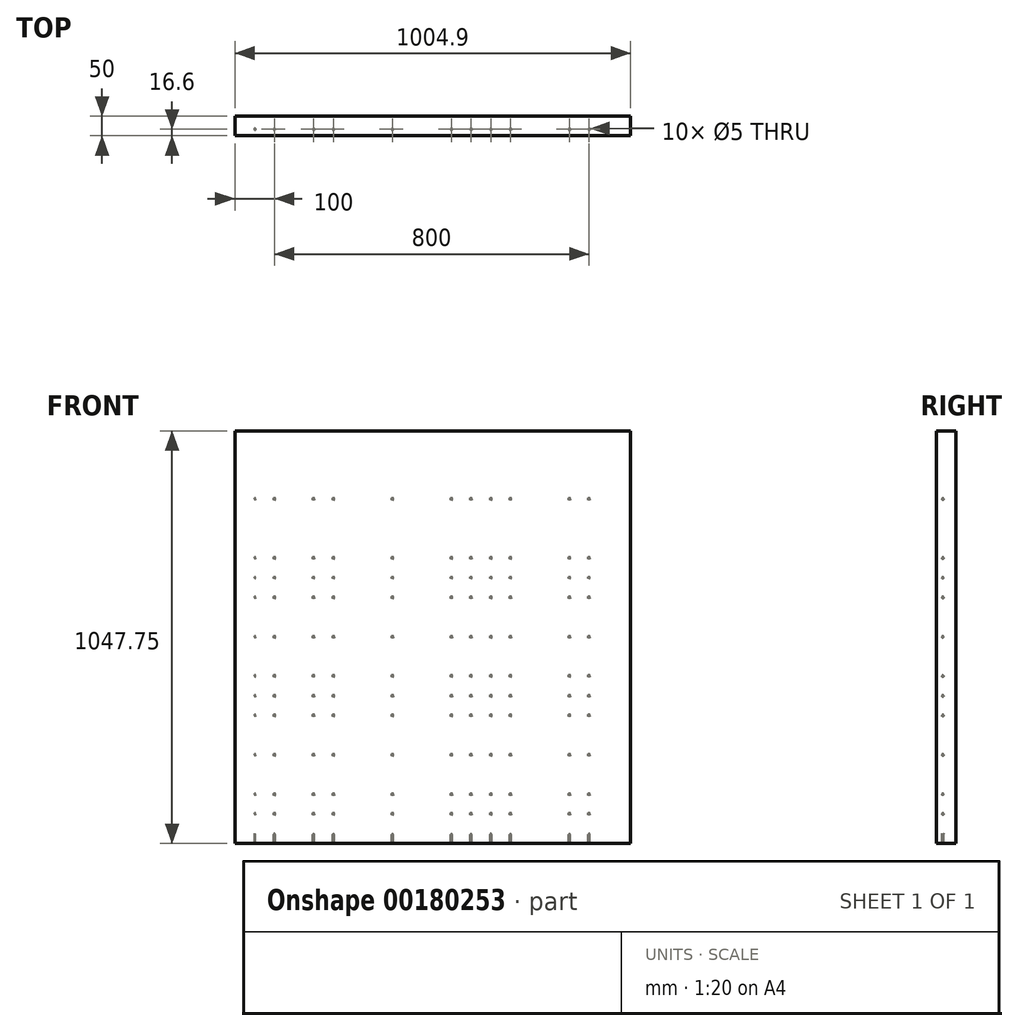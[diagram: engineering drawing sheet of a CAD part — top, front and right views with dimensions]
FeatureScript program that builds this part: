
annotation { "Feature Type Name" : "Feature", "Feature Type Description" : "" }
export const myFeature = defineFeature(function(context is Context, id is Id, definition is map)
    precondition{}
    {
        {
            var Q0;
            Q0=qCreatedBy(makeId("Right.planeOp"),FACE);
            var sketch = newSketch(context, id + "F0", { "sketchPlane" : qUnion([Q0])});
            skLineSegment(sketch, "E0.bottom", {"start": v(25, 516.75) * mm, "end": v(-25, 516.75) * mm});
            skLineSegment(sketch, "E0.top", {"start": v(25, -531) * mm, "end": v(-25, -531) * mm});
            skLineSegment(sketch, "E0.left", {"start": v(25, 516.75) * mm, "end": v(25, -531) * mm});
            skLineSegment(sketch, "E0.right", {"start": v(-25, 516.75) * mm, "end": v(-25, -531) * mm});
            skPoint(sketch, "E0.middle", {"position": v(0, -7.13) * mm});
            skLineSegment(sketch, "E1.0", {"start": v(25, -506) * mm, "end": v(-25, -506) * mm});
            skLineSegment(sketch, "E2.0", {"start": v(-8.4, 516.75) * mm, "end": v(-8.4, -531) * mm});
            skCircle(sketch, "E3", {"center": v(-8.4, -506) * mm, "radius": 2.5 * mm});
            skCircle(sketch, "E4.0.1.0", {"center": v(-8.4, -456) * mm, "radius": 2.5 * mm});
            skCircle(sketch, "E4.0.2.0", {"center": v(-8.4, -406) * mm, "radius": 2.5 * mm});
            skCircle(sketch, "E4.0.3.0", {"center": v(-8.4, -356) * mm, "radius": 2.5 * mm});
            skCircle(sketch, "E4.0.4.0", {"center": v(-8.4, -306) * mm, "radius": 2.5 * mm});
            skCircle(sketch, "E4.0.5.0", {"center": v(-8.4, -256) * mm, "radius": 2.5 * mm});
            skCircle(sketch, "E4.0.6.0", {"center": v(-8.4, -206) * mm, "radius": 2.5 * mm});
            skCircle(sketch, "E4.0.7.0", {"center": v(-8.4, -156) * mm, "radius": 2.5 * mm});
            skCircle(sketch, "E4.0.8.0", {"center": v(-8.4, -106) * mm, "radius": 2.5 * mm});
            skCircle(sketch, "E4.0.9.0", {"center": v(-8.4, -56) * mm, "radius": 2.5 * mm});
            skCircle(sketch, "E4.0.10.0", {"center": v(-8.4, -6) * mm, "radius": 2.5 * mm});
            skCircle(sketch, "E4.0.11.0", {"center": v(-8.4, 44) * mm, "radius": 2.5 * mm});
            skCircle(sketch, "E4.0.12.0", {"center": v(-8.4, 94) * mm, "radius": 2.5 * mm});
            skCircle(sketch, "E4.0.13.0", {"center": v(-8.4, 144) * mm, "radius": 2.5 * mm});
            skCircle(sketch, "E4.0.14.0", {"center": v(-8.4, 194) * mm, "radius": 2.5 * mm});
            skCircle(sketch, "E4.0.15.0", {"center": v(-8.4, 244) * mm, "radius": 2.5 * mm});
            skCircle(sketch, "E4.0.16.0", {"center": v(-8.4, 294) * mm, "radius": 2.5 * mm});
            skCircle(sketch, "E4.0.17.0", {"center": v(-8.4, 344) * mm, "radius": 2.5 * mm});
            skCircle(sketch, "E4.0.18.0", {"center": v(-8.4, 394) * mm, "radius": 2.5 * mm});
            skCircle(sketch, "E4.0.19.0", {"center": v(-8.4, 444) * mm, "radius": 2.5 * mm});
            skLineSegment(sketch, "E4.direction1", {"start": v(-8.4, -506) * mm, "end": v(16.6, -506) * mm, "construction": true});
            skLineSegment(sketch, "E4.direction2", {"start": v(-8.4, -506) * mm, "end": v(-8.4, -456) * mm, "construction": true});
            skLineSegment(sketch, "E5", {"start": v(0, 0) * mm, "end": v(63.1, 0) * mm});
            skSolve(sketch);
        }
        {
            var Q0;
            Q0=qCreatedBy(makeId("Top.planeOp"),FACE);
            cPlane(context, id + "F1", {"entities" : qUnion([Q0]), "cplaneType" : CPlaneType.OFFSET, "offset" : 466.6 * mm, "width" : 150 * mm, "height" : 150 * mm});
        }
        {
            var Q0;
            Q0=qCreatedBy(id+"F1.planeOp",FACE);
            var sketch = newSketch(context, id + "F2", { "sketchPlane" : qUnion([Q0])});
            skLineSegment(sketch, "E6.bottom", {"start": v(1004.9, -25) * mm, "end": v(0, -25) * mm});
            skLineSegment(sketch, "E6.top", {"start": v(1004.9, 25) * mm, "end": v(0, 25) * mm});
            skLineSegment(sketch, "E6.left", {"start": v(1004.9, -25) * mm, "end": v(1004.9, 25) * mm});
            skLineSegment(sketch, "E6.right", {"start": v(0, -25) * mm, "end": v(0, 25) * mm});
            skPoint(sketch, "E6.middle", {"position": v(502.45, 0) * mm});
            skLineSegment(sketch, "E7", {"start": v(0, 25) * mm, "end": v(51.84, 25) * mm});
            skLineSegment(sketch, "E8", {"start": v(0, 25) * mm, "end": v(0, 69.64) * mm});
            skLineSegment(sketch, "E9.0", {"start": v(1004.9, -8.4) * mm, "end": v(0, -8.4) * mm});
            skLineSegment(sketch, "E10.0", {"start": v(50, -25) * mm, "end": v(50, 25) * mm});
            skCircle(sketch, "E11", {"center": v(50, -8.4) * mm, "radius": 2.5 * mm});
            skCircle(sketch, "E12.1.0.0", {"center": v(100, -8.4) * mm, "radius": 2.5 * mm});
            skCircle(sketch, "E12.2.0.0", {"center": v(150, -8.4) * mm, "radius": 2.5 * mm});
            skCircle(sketch, "E12.3.0.0", {"center": v(200, -8.4) * mm, "radius": 2.5 * mm});
            skCircle(sketch, "E12.4.0.0", {"center": v(250, -8.4) * mm, "radius": 2.5 * mm});
            skCircle(sketch, "E12.5.0.0", {"center": v(300, -8.4) * mm, "radius": 2.5 * mm});
            skCircle(sketch, "E12.6.0.0", {"center": v(350, -8.4) * mm, "radius": 2.5 * mm});
            skCircle(sketch, "E12.7.0.0", {"center": v(400, -8.4) * mm, "radius": 2.5 * mm});
            skCircle(sketch, "E12.8.0.0", {"center": v(450, -8.4) * mm, "radius": 2.5 * mm});
            skCircle(sketch, "E12.9.0.0", {"center": v(500, -8.4) * mm, "radius": 2.5 * mm});
            skCircle(sketch, "E12.10.0.0", {"center": v(550, -8.4) * mm, "radius": 2.5 * mm});
            skCircle(sketch, "E12.11.0.0", {"center": v(600, -8.4) * mm, "radius": 2.5 * mm});
            skCircle(sketch, "E12.12.0.0", {"center": v(650, -8.4) * mm, "radius": 2.5 * mm});
            skCircle(sketch, "E12.13.0.0", {"center": v(700, -8.4) * mm, "radius": 2.5 * mm});
            skCircle(sketch, "E12.14.0.0", {"center": v(750, -8.4) * mm, "radius": 2.5 * mm});
            skCircle(sketch, "E12.15.0.0", {"center": v(800, -8.4) * mm, "radius": 2.5 * mm});
            skCircle(sketch, "E12.16.0.0", {"center": v(850, -8.4) * mm, "radius": 2.5 * mm});
            skCircle(sketch, "E12.17.0.0", {"center": v(900, -8.4) * mm, "radius": 2.5 * mm});
            skCircle(sketch, "E12.18.0.0", {"center": v(950, -8.4) * mm, "radius": 2.5 * mm});
            skLineSegment(sketch, "E12.direction1", {"start": v(50, -8.4) * mm, "end": v(100, -8.4) * mm, "construction": true});
            skSolve(sketch);
        }
        {
            var Q0;
            {var subQ0=sQuery(id+"F0.wireOp",EDGE,"E4.0.18.0");var subQ1=sQuery(id+"F0.wireOp",EDGE,"E2.0");var subQ2=makeQuery(id+"F0.imprint","INTERSECT",VERTEX,{"disambiguationData":[OD(0.0)],"derivedFrom":[subQ1,subQ0]});Q0=makeQuery(id+"F0.imprint","IMPRINT",FACE,{"disambiguationData":[TD([[makeQuery(id+"F0.imprint","IMPRINT",EDGE,{"disambiguationData":[TD([[subQ2,-1.0]])],"derivedFrom":subQ1}),-1.0]])]});}
            var Q1;
            {var subQ0=sQuery(id+"F0.wireOp",EDGE,"E4.0.19.0");var subQ1=sQuery(id+"F0.wireOp",EDGE,"E2.0");var subQ2=makeQuery(id+"F0.imprint","INTERSECT",VERTEX,{"disambiguationData":[OD(0.0)],"derivedFrom":[subQ1,subQ0]});Q1=makeQuery(id+"F0.imprint","IMPRINT",FACE,{"disambiguationData":[TD([[makeQuery(id+"F0.imprint","IMPRINT",EDGE,{"disambiguationData":[TD([[subQ2,-1.0]])],"derivedFrom":subQ1}),1.0]])]});}
            var Q2;
            {var subQ0=sQuery(id+"F0.wireOp",EDGE,"E4.0.19.0");var subQ1=sQuery(id+"F0.wireOp",EDGE,"E2.0");var subQ2=makeQuery(id+"F0.imprint","INTERSECT",VERTEX,{"disambiguationData":[OD(0.0)],"derivedFrom":[subQ1,subQ0]});Q2=makeQuery(id+"F0.imprint","IMPRINT",FACE,{"disambiguationData":[TD([[makeQuery(id+"F0.imprint","IMPRINT",EDGE,{"disambiguationData":[TD([[subQ2,-1.0]])],"derivedFrom":subQ1}),-1.0]])]});}
            var Q3;
            {var subQ0=sQuery(id+"F0.wireOp",EDGE,"E4.0.17.0");var subQ1=sQuery(id+"F0.wireOp",EDGE,"E2.0");var subQ2=makeQuery(id+"F0.imprint","INTERSECT",VERTEX,{"disambiguationData":[OD(0.0)],"derivedFrom":[subQ1,subQ0]});Q3=makeQuery(id+"F0.imprint","IMPRINT",FACE,{"disambiguationData":[TD([[makeQuery(id+"F0.imprint","IMPRINT",EDGE,{"disambiguationData":[TD([[subQ2,-1.0]])],"derivedFrom":subQ1}),1.0]])]});}
            var Q4;
            {var subQ0=sQuery(id+"F0.wireOp",EDGE,"E4.0.17.0");var subQ1=sQuery(id+"F0.wireOp",EDGE,"E2.0");var subQ2=makeQuery(id+"F0.imprint","INTERSECT",VERTEX,{"disambiguationData":[OD(0.0)],"derivedFrom":[subQ1,subQ0]});Q4=makeQuery(id+"F0.imprint","IMPRINT",FACE,{"disambiguationData":[TD([[makeQuery(id+"F0.imprint","IMPRINT",EDGE,{"disambiguationData":[TD([[subQ2,-1.0]])],"derivedFrom":subQ1}),-1.0]])]});}
            var Q5;
            {var subQ0=sQuery(id+"F0.wireOp",EDGE,"E4.0.18.0");var subQ1=sQuery(id+"F0.wireOp",EDGE,"E2.0");var subQ2=makeQuery(id+"F0.imprint","INTERSECT",VERTEX,{"disambiguationData":[OD(0.0)],"derivedFrom":[subQ1,subQ0]});Q5=makeQuery(id+"F0.imprint","IMPRINT",FACE,{"disambiguationData":[TD([[makeQuery(id+"F0.imprint","IMPRINT",EDGE,{"disambiguationData":[TD([[subQ2,-1.0]])],"derivedFrom":subQ1}),1.0]])]});}
            var Q6;
            {var subQ0=sQuery(id+"F0.wireOp",EDGE,"E4.0.16.0");var subQ1=sQuery(id+"F0.wireOp",EDGE,"E2.0");var subQ2=makeQuery(id+"F0.imprint","INTERSECT",VERTEX,{"disambiguationData":[OD(0.0)],"derivedFrom":[subQ1,subQ0]});Q6=makeQuery(id+"F0.imprint","IMPRINT",FACE,{"disambiguationData":[TD([[makeQuery(id+"F0.imprint","IMPRINT",EDGE,{"disambiguationData":[TD([[subQ2,-1.0]])],"derivedFrom":subQ1}),1.0]])]});}
            var Q7;
            {var subQ0=sQuery(id+"F0.wireOp",EDGE,"E4.0.16.0");var subQ1=sQuery(id+"F0.wireOp",EDGE,"E2.0");var subQ2=makeQuery(id+"F0.imprint","INTERSECT",VERTEX,{"disambiguationData":[OD(0.0)],"derivedFrom":[subQ1,subQ0]});Q7=makeQuery(id+"F0.imprint","IMPRINT",FACE,{"disambiguationData":[TD([[makeQuery(id+"F0.imprint","IMPRINT",EDGE,{"disambiguationData":[TD([[subQ2,-1.0]])],"derivedFrom":subQ1}),-1.0]])]});}
            var Q8;
            {var subQ0=sQuery(id+"F0.wireOp",EDGE,"E4.0.15.0");var subQ1=sQuery(id+"F0.wireOp",EDGE,"E2.0");var subQ2=makeQuery(id+"F0.imprint","INTERSECT",VERTEX,{"disambiguationData":[OD(0.0)],"derivedFrom":[subQ1,subQ0]});Q8=makeQuery(id+"F0.imprint","IMPRINT",FACE,{"disambiguationData":[TD([[makeQuery(id+"F0.imprint","IMPRINT",EDGE,{"disambiguationData":[TD([[subQ2,-1.0]])],"derivedFrom":subQ1}),1.0]])]});}
            var Q9;
            {var subQ0=sQuery(id+"F0.wireOp",EDGE,"E4.0.14.0");var subQ1=sQuery(id+"F0.wireOp",EDGE,"E2.0");var subQ2=makeQuery(id+"F0.imprint","INTERSECT",VERTEX,{"disambiguationData":[OD(0.0)],"derivedFrom":[subQ1,subQ0]});Q9=makeQuery(id+"F0.imprint","IMPRINT",FACE,{"disambiguationData":[TD([[makeQuery(id+"F0.imprint","IMPRINT",EDGE,{"disambiguationData":[TD([[subQ2,-1.0]])],"derivedFrom":subQ1}),-1.0]])]});}
            var Q10;
            {var subQ0=sQuery(id+"F0.wireOp",EDGE,"E4.0.15.0");var subQ1=sQuery(id+"F0.wireOp",EDGE,"E2.0");var subQ2=makeQuery(id+"F0.imprint","INTERSECT",VERTEX,{"disambiguationData":[OD(0.0)],"derivedFrom":[subQ1,subQ0]});Q10=makeQuery(id+"F0.imprint","IMPRINT",FACE,{"disambiguationData":[TD([[makeQuery(id+"F0.imprint","IMPRINT",EDGE,{"disambiguationData":[TD([[subQ2,-1.0]])],"derivedFrom":subQ1}),-1.0]])]});}
            var Q11;
            {var subQ0=sQuery(id+"F0.wireOp",EDGE,"E4.0.13.0");var subQ1=sQuery(id+"F0.wireOp",EDGE,"E2.0");var subQ2=makeQuery(id+"F0.imprint","INTERSECT",VERTEX,{"disambiguationData":[OD(0.0)],"derivedFrom":[subQ1,subQ0]});Q11=makeQuery(id+"F0.imprint","IMPRINT",FACE,{"disambiguationData":[TD([[makeQuery(id+"F0.imprint","IMPRINT",EDGE,{"disambiguationData":[TD([[subQ2,-1.0]])],"derivedFrom":subQ1}),1.0]])]});}
            var Q12;
            {var subQ0=sQuery(id+"F0.wireOp",EDGE,"E4.0.14.0");var subQ1=sQuery(id+"F0.wireOp",EDGE,"E2.0");var subQ2=makeQuery(id+"F0.imprint","INTERSECT",VERTEX,{"disambiguationData":[OD(0.0)],"derivedFrom":[subQ1,subQ0]});Q12=makeQuery(id+"F0.imprint","IMPRINT",FACE,{"disambiguationData":[TD([[makeQuery(id+"F0.imprint","IMPRINT",EDGE,{"disambiguationData":[TD([[subQ2,-1.0]])],"derivedFrom":subQ1}),1.0]])]});}
            var Q13;
            {var subQ0=sQuery(id+"F0.wireOp",EDGE,"E4.0.13.0");var subQ1=sQuery(id+"F0.wireOp",EDGE,"E2.0");var subQ2=makeQuery(id+"F0.imprint","INTERSECT",VERTEX,{"disambiguationData":[OD(0.0)],"derivedFrom":[subQ1,subQ0]});Q13=makeQuery(id+"F0.imprint","IMPRINT",FACE,{"disambiguationData":[TD([[makeQuery(id+"F0.imprint","IMPRINT",EDGE,{"disambiguationData":[TD([[subQ2,-1.0]])],"derivedFrom":subQ1}),-1.0]])]});}
            var Q14;
            {var subQ0=sQuery(id+"F0.wireOp",EDGE,"E4.0.9.0");var subQ1=sQuery(id+"F0.wireOp",EDGE,"E2.0");var subQ2=makeQuery(id+"F0.imprint","INTERSECT",VERTEX,{"disambiguationData":[OD(0.0)],"derivedFrom":[subQ1,subQ0]});Q14=makeQuery(id+"F0.imprint","IMPRINT",FACE,{"disambiguationData":[TD([[makeQuery(id+"F0.imprint","IMPRINT",EDGE,{"disambiguationData":[TD([[subQ2,-1.0]])],"derivedFrom":subQ1}),1.0]])]});}
            var Q15;
            {var subQ0=sQuery(id+"F0.wireOp",EDGE,"E4.0.9.0");var subQ1=sQuery(id+"F0.wireOp",EDGE,"E2.0");var subQ2=makeQuery(id+"F0.imprint","INTERSECT",VERTEX,{"disambiguationData":[OD(0.0)],"derivedFrom":[subQ1,subQ0]});Q15=makeQuery(id+"F0.imprint","IMPRINT",FACE,{"disambiguationData":[TD([[makeQuery(id+"F0.imprint","IMPRINT",EDGE,{"disambiguationData":[TD([[subQ2,-1.0]])],"derivedFrom":subQ1}),-1.0]])]});}
            var Q16;
            {var subQ0=sQuery(id+"F0.wireOp",EDGE,"E4.0.10.0");var subQ1=sQuery(id+"F0.wireOp",EDGE,"E2.0");var subQ2=makeQuery(id+"F0.imprint","INTERSECT",VERTEX,{"disambiguationData":[OD(0.0)],"derivedFrom":[subQ1,subQ0]});Q16=makeQuery(id+"F0.imprint","IMPRINT",FACE,{"disambiguationData":[TD([[makeQuery(id+"F0.imprint","IMPRINT",EDGE,{"disambiguationData":[TD([[subQ2,-1.0]])],"derivedFrom":subQ1}),-1.0]])]});}
            var Q17;
            {var subQ0=sQuery(id+"F0.wireOp",EDGE,"E4.0.12.0");var subQ1=sQuery(id+"F0.wireOp",EDGE,"E2.0");var subQ2=makeQuery(id+"F0.imprint","INTERSECT",VERTEX,{"disambiguationData":[OD(0.0)],"derivedFrom":[subQ1,subQ0]});Q17=makeQuery(id+"F0.imprint","IMPRINT",FACE,{"disambiguationData":[TD([[makeQuery(id+"F0.imprint","IMPRINT",EDGE,{"disambiguationData":[TD([[subQ2,-1.0]])],"derivedFrom":subQ1}),1.0]])]});}
            var Q18;
            {var subQ0=sQuery(id+"F0.wireOp",EDGE,"E4.0.6.0");var subQ1=sQuery(id+"F0.wireOp",EDGE,"E2.0");var subQ2=makeQuery(id+"F0.imprint","INTERSECT",VERTEX,{"disambiguationData":[OD(0.0)],"derivedFrom":[subQ1,subQ0]});Q18=makeQuery(id+"F0.imprint","IMPRINT",FACE,{"disambiguationData":[TD([[makeQuery(id+"F0.imprint","IMPRINT",EDGE,{"disambiguationData":[TD([[subQ2,-1.0]])],"derivedFrom":subQ1}),-1.0]])]});}
            var Q19;
            {var subQ0=sQuery(id+"F0.wireOp",EDGE,"E4.0.11.0");var subQ1=sQuery(id+"F0.wireOp",EDGE,"E2.0");var subQ2=makeQuery(id+"F0.imprint","INTERSECT",VERTEX,{"disambiguationData":[OD(0.0)],"derivedFrom":[subQ1,subQ0]});Q19=makeQuery(id+"F0.imprint","IMPRINT",FACE,{"disambiguationData":[TD([[makeQuery(id+"F0.imprint","IMPRINT",EDGE,{"disambiguationData":[TD([[subQ2,-1.0]])],"derivedFrom":subQ1}),1.0]])]});}
            var Q20;
            {var subQ0=sQuery(id+"F0.wireOp",EDGE,"E4.0.10.0");var subQ1=sQuery(id+"F0.wireOp",EDGE,"E2.0");var subQ2=makeQuery(id+"F0.imprint","INTERSECT",VERTEX,{"disambiguationData":[OD(0.0)],"derivedFrom":[subQ1,subQ0]});Q20=makeQuery(id+"F0.imprint","IMPRINT",FACE,{"disambiguationData":[TD([[makeQuery(id+"F0.imprint","IMPRINT",EDGE,{"disambiguationData":[TD([[subQ2,-1.0]])],"derivedFrom":subQ1}),1.0]])]});}
            var Q21;
            {var subQ0=sQuery(id+"F0.wireOp",EDGE,"E4.0.7.0");var subQ1=sQuery(id+"F0.wireOp",EDGE,"E2.0");var subQ2=makeQuery(id+"F0.imprint","INTERSECT",VERTEX,{"disambiguationData":[OD(0.0)],"derivedFrom":[subQ1,subQ0]});Q21=makeQuery(id+"F0.imprint","IMPRINT",FACE,{"disambiguationData":[TD([[makeQuery(id+"F0.imprint","IMPRINT",EDGE,{"disambiguationData":[TD([[subQ2,-1.0]])],"derivedFrom":subQ1}),-1.0]])]});}
            var Q22;
            {var subQ0=sQuery(id+"F0.wireOp",EDGE,"E4.0.8.0");var subQ1=sQuery(id+"F0.wireOp",EDGE,"E2.0");var subQ2=makeQuery(id+"F0.imprint","INTERSECT",VERTEX,{"disambiguationData":[OD(0.0)],"derivedFrom":[subQ1,subQ0]});Q22=makeQuery(id+"F0.imprint","IMPRINT",FACE,{"disambiguationData":[TD([[makeQuery(id+"F0.imprint","IMPRINT",EDGE,{"disambiguationData":[TD([[subQ2,-1.0]])],"derivedFrom":subQ1}),-1.0]])]});}
            var Q23;
            {var subQ0=sQuery(id+"F0.wireOp",EDGE,"E4.0.11.0");var subQ1=sQuery(id+"F0.wireOp",EDGE,"E2.0");var subQ2=makeQuery(id+"F0.imprint","INTERSECT",VERTEX,{"disambiguationData":[OD(0.0)],"derivedFrom":[subQ1,subQ0]});Q23=makeQuery(id+"F0.imprint","IMPRINT",FACE,{"disambiguationData":[TD([[makeQuery(id+"F0.imprint","IMPRINT",EDGE,{"disambiguationData":[TD([[subQ2,-1.0]])],"derivedFrom":subQ1}),-1.0]])]});}
            var Q24;
            {var subQ0=sQuery(id+"F0.wireOp",EDGE,"E4.0.12.0");var subQ1=sQuery(id+"F0.wireOp",EDGE,"E2.0");var subQ2=makeQuery(id+"F0.imprint","INTERSECT",VERTEX,{"disambiguationData":[OD(0.0)],"derivedFrom":[subQ1,subQ0]});Q24=makeQuery(id+"F0.imprint","IMPRINT",FACE,{"disambiguationData":[TD([[makeQuery(id+"F0.imprint","IMPRINT",EDGE,{"disambiguationData":[TD([[subQ2,-1.0]])],"derivedFrom":subQ1}),-1.0]])]});}
            var Q25;
            {var subQ0=sQuery(id+"F0.wireOp",EDGE,"E4.0.6.0");var subQ1=sQuery(id+"F0.wireOp",EDGE,"E2.0");var subQ2=makeQuery(id+"F0.imprint","INTERSECT",VERTEX,{"disambiguationData":[OD(0.0)],"derivedFrom":[subQ1,subQ0]});Q25=makeQuery(id+"F0.imprint","IMPRINT",FACE,{"disambiguationData":[TD([[makeQuery(id+"F0.imprint","IMPRINT",EDGE,{"disambiguationData":[TD([[subQ2,-1.0]])],"derivedFrom":subQ1}),1.0]])]});}
            var Q26;
            {var subQ0=sQuery(id+"F0.wireOp",EDGE,"E4.0.7.0");var subQ1=sQuery(id+"F0.wireOp",EDGE,"E2.0");var subQ2=makeQuery(id+"F0.imprint","INTERSECT",VERTEX,{"disambiguationData":[OD(0.0)],"derivedFrom":[subQ1,subQ0]});Q26=makeQuery(id+"F0.imprint","IMPRINT",FACE,{"disambiguationData":[TD([[makeQuery(id+"F0.imprint","IMPRINT",EDGE,{"disambiguationData":[TD([[subQ2,-1.0]])],"derivedFrom":subQ1}),1.0]])]});}
            var Q27;
            {var subQ0=sQuery(id+"F0.wireOp",EDGE,"E4.0.8.0");var subQ1=sQuery(id+"F0.wireOp",EDGE,"E2.0");var subQ2=makeQuery(id+"F0.imprint","INTERSECT",VERTEX,{"disambiguationData":[OD(0.0)],"derivedFrom":[subQ1,subQ0]});Q27=makeQuery(id+"F0.imprint","IMPRINT",FACE,{"disambiguationData":[TD([[makeQuery(id+"F0.imprint","IMPRINT",EDGE,{"disambiguationData":[TD([[subQ2,-1.0]])],"derivedFrom":subQ1}),1.0]])]});}
            var Q28;
            {var subQ0=sQuery(id+"F0.wireOp",EDGE,"E4.0.3.0");var subQ1=sQuery(id+"F0.wireOp",EDGE,"E2.0");var subQ2=makeQuery(id+"F0.imprint","INTERSECT",VERTEX,{"disambiguationData":[OD(0.0)],"derivedFrom":[subQ1,subQ0]});Q28=makeQuery(id+"F0.imprint","IMPRINT",FACE,{"disambiguationData":[TD([[makeQuery(id+"F0.imprint","IMPRINT",EDGE,{"disambiguationData":[TD([[subQ2,-1.0]])],"derivedFrom":subQ1}),-1.0]])]});}
            var Q29;
            {var subQ0=sQuery(id+"F0.wireOp",EDGE,"E4.0.4.0");var subQ1=sQuery(id+"F0.wireOp",EDGE,"E2.0");var subQ2=makeQuery(id+"F0.imprint","INTERSECT",VERTEX,{"disambiguationData":[OD(0.0)],"derivedFrom":[subQ1,subQ0]});Q29=makeQuery(id+"F0.imprint","IMPRINT",FACE,{"disambiguationData":[TD([[makeQuery(id+"F0.imprint","IMPRINT",EDGE,{"disambiguationData":[TD([[subQ2,-1.0]])],"derivedFrom":subQ1}),-1.0]])]});}
            var Q30;
            {var subQ0=sQuery(id+"F0.wireOp",EDGE,"E4.0.3.0");var subQ1=sQuery(id+"F0.wireOp",EDGE,"E2.0");var subQ2=makeQuery(id+"F0.imprint","INTERSECT",VERTEX,{"disambiguationData":[OD(0.0)],"derivedFrom":[subQ1,subQ0]});Q30=makeQuery(id+"F0.imprint","IMPRINT",FACE,{"disambiguationData":[TD([[makeQuery(id+"F0.imprint","IMPRINT",EDGE,{"disambiguationData":[TD([[subQ2,-1.0]])],"derivedFrom":subQ1}),1.0]])]});}
            var Q31;
            {var subQ0=sQuery(id+"F0.wireOp",EDGE,"E4.0.5.0");var subQ1=sQuery(id+"F0.wireOp",EDGE,"E2.0");var subQ2=makeQuery(id+"F0.imprint","INTERSECT",VERTEX,{"disambiguationData":[OD(0.0)],"derivedFrom":[subQ1,subQ0]});Q31=makeQuery(id+"F0.imprint","IMPRINT",FACE,{"disambiguationData":[TD([[makeQuery(id+"F0.imprint","IMPRINT",EDGE,{"disambiguationData":[TD([[subQ2,-1.0]])],"derivedFrom":subQ1}),-1.0]])]});}
            var Q32;
            {var subQ0=sQuery(id+"F0.wireOp",EDGE,"E4.0.5.0");var subQ1=sQuery(id+"F0.wireOp",EDGE,"E2.0");var subQ2=makeQuery(id+"F0.imprint","INTERSECT",VERTEX,{"disambiguationData":[OD(0.0)],"derivedFrom":[subQ1,subQ0]});Q32=makeQuery(id+"F0.imprint","IMPRINT",FACE,{"disambiguationData":[TD([[makeQuery(id+"F0.imprint","IMPRINT",EDGE,{"disambiguationData":[TD([[subQ2,-1.0]])],"derivedFrom":subQ1}),1.0]])]});}
            var Q33;
            {var subQ0=sQuery(id+"F0.wireOp",EDGE,"E4.0.2.0");var subQ1=sQuery(id+"F0.wireOp",EDGE,"E2.0");var subQ2=makeQuery(id+"F0.imprint","INTERSECT",VERTEX,{"disambiguationData":[OD(0.0)],"derivedFrom":[subQ1,subQ0]});Q33=makeQuery(id+"F0.imprint","IMPRINT",FACE,{"disambiguationData":[TD([[makeQuery(id+"F0.imprint","IMPRINT",EDGE,{"disambiguationData":[TD([[subQ2,-1.0]])],"derivedFrom":subQ1}),1.0]])]});}
            var Q34;
            {var subQ0=sQuery(id+"F0.wireOp",EDGE,"E4.0.2.0");var subQ1=sQuery(id+"F0.wireOp",EDGE,"E2.0");var subQ2=makeQuery(id+"F0.imprint","INTERSECT",VERTEX,{"disambiguationData":[OD(0.0)],"derivedFrom":[subQ1,subQ0]});Q34=makeQuery(id+"F0.imprint","IMPRINT",FACE,{"disambiguationData":[TD([[makeQuery(id+"F0.imprint","IMPRINT",EDGE,{"disambiguationData":[TD([[subQ2,-1.0]])],"derivedFrom":subQ1}),-1.0]])]});}
            var Q35;
            {var subQ0=sQuery(id+"F0.wireOp",EDGE,"E4.0.4.0");var subQ1=sQuery(id+"F0.wireOp",EDGE,"E2.0");var subQ2=makeQuery(id+"F0.imprint","INTERSECT",VERTEX,{"disambiguationData":[OD(0.0)],"derivedFrom":[subQ1,subQ0]});Q35=makeQuery(id+"F0.imprint","IMPRINT",FACE,{"disambiguationData":[TD([[makeQuery(id+"F0.imprint","IMPRINT",EDGE,{"disambiguationData":[TD([[subQ2,-1.0]])],"derivedFrom":subQ1}),1.0]])]});}
            var Q36;
            {var subQ0=sQuery(id+"F0.wireOp",EDGE,"E4.0.1.0");var subQ1=sQuery(id+"F0.wireOp",EDGE,"E2.0");var subQ2=makeQuery(id+"F0.imprint","INTERSECT",VERTEX,{"disambiguationData":[OD(0.0)],"derivedFrom":[subQ1,subQ0]});Q36=makeQuery(id+"F0.imprint","IMPRINT",FACE,{"disambiguationData":[TD([[makeQuery(id+"F0.imprint","IMPRINT",EDGE,{"disambiguationData":[TD([[subQ2,-1.0]])],"derivedFrom":subQ1}),1.0]])]});}
            var Q37;
            {var subQ0=sQuery(id+"F0.wireOp",EDGE,"E4.0.1.0");var subQ1=sQuery(id+"F0.wireOp",EDGE,"E2.0");var subQ2=makeQuery(id+"F0.imprint","INTERSECT",VERTEX,{"disambiguationData":[OD(0.0)],"derivedFrom":[subQ1,subQ0]});Q37=makeQuery(id+"F0.imprint","IMPRINT",FACE,{"disambiguationData":[TD([[makeQuery(id+"F0.imprint","IMPRINT",EDGE,{"disambiguationData":[TD([[subQ2,-1.0]])],"derivedFrom":subQ1}),-1.0]])]});}
            var Q38;
            {var subQ0=sQuery(id+"F0.wireOp",EDGE,"E2.0");var subQ1=sQuery(id+"F0.wireOp",EDGE,"E1.0");var subQ2=makeQuery(id+"F0.imprint","INTERSECT",VERTEX,{"derivedFrom":[subQ1,subQ0]});Q38=makeQuery(id+"F0.imprint","IMPRINT",FACE,{"disambiguationData":[TD([[makeQuery(id+"F0.imprint","IMPRINT",EDGE,{"disambiguationData":[TD([[subQ2,-1.0]])],"derivedFrom":subQ1}),-1.0]])]});}
            var Q39;
            {var subQ0=sQuery(id+"F0.wireOp",EDGE,"E3");var subQ1=sQuery(id+"F0.wireOp",EDGE,"E1.0");var subQ2=makeQuery(id+"F0.imprint","INTERSECT",VERTEX,{"disambiguationData":[OD(0.0)],"derivedFrom":[subQ1,subQ0]});Q39=makeQuery(id+"F0.imprint","IMPRINT",FACE,{"disambiguationData":[TD([[makeQuery(id+"F0.imprint","IMPRINT",EDGE,{"disambiguationData":[TD([[subQ2,-1.0]])],"derivedFrom":subQ1}),-1.0]])]});}
            var Q40;
            {var subQ0=sQuery(id+"F0.wireOp",EDGE,"E2.0");var subQ1=sQuery(id+"F0.wireOp",EDGE,"E1.0");var subQ2=makeQuery(id+"F0.imprint","INTERSECT",VERTEX,{"derivedFrom":[subQ1,subQ0]});Q40=makeQuery(id+"F0.imprint","IMPRINT",FACE,{"disambiguationData":[TD([[makeQuery(id+"F0.imprint","IMPRINT",EDGE,{"disambiguationData":[TD([[subQ2,-1.0]])],"derivedFrom":subQ1}),1.0]])]});}
            var Q41;
            {var subQ0=sQuery(id+"F0.wireOp",EDGE,"E3");var subQ1=sQuery(id+"F0.wireOp",EDGE,"E1.0");var subQ2=makeQuery(id+"F0.imprint","INTERSECT",VERTEX,{"disambiguationData":[OD(0.0)],"derivedFrom":[subQ1,subQ0]});Q41=makeQuery(id+"F0.imprint","IMPRINT",FACE,{"disambiguationData":[TD([[makeQuery(id+"F0.imprint","IMPRINT",EDGE,{"disambiguationData":[TD([[subQ2,-1.0]])],"derivedFrom":subQ1}),1.0]])]});}
            extrude(context, id + "F3", {"entities" : qUnion([Q0, Q1, Q2, Q3, Q4, Q5, Q6, Q7, Q8, Q9, Q10, Q11, Q12, Q13, Q14, Q15, Q16, Q17, Q18, Q19, Q20, Q21, Q22, Q23, Q24, Q25, Q26, Q27, Q28, Q29, Q30, Q31, Q32, Q33, Q34, Q35, Q36, Q37, Q38, Q39, Q40, Q41]), "depth" : 1004.9 * mm});
        }
        {
            var Q0;
            {var subQ0=sQuery(id+"F2.wireOp",EDGE,"E11");var subQ1=sQuery(id+"F2.wireOp",EDGE,"E9.0");var subQ2=makeQuery(id+"F2.imprint","INTERSECT",VERTEX,{"disambiguationData":[OD(0.0)],"derivedFrom":[subQ1,subQ0]});Q0=makeQuery(id+"F2.imprint","IMPRINT",FACE,{"disambiguationData":[TD([[makeQuery(id+"F2.imprint","IMPRINT",EDGE,{"disambiguationData":[TD([[subQ2,-1.0]])],"derivedFrom":subQ1}),1.0]])]});}
            var Q1;
            {var subQ0=sQuery(id+"F2.wireOp",EDGE,"E10.0");var subQ1=sQuery(id+"F2.wireOp",EDGE,"E9.0");var subQ2=makeQuery(id+"F2.imprint","INTERSECT",VERTEX,{"derivedFrom":[subQ1,subQ0]});Q1=makeQuery(id+"F2.imprint","IMPRINT",FACE,{"disambiguationData":[TD([[makeQuery(id+"F2.imprint","IMPRINT",EDGE,{"disambiguationData":[TD([[subQ2,-1.0]])],"derivedFrom":subQ1}),1.0]])]});}
            var Q2;
            {var subQ0=sQuery(id+"F2.wireOp",EDGE,"E10.0");var subQ1=sQuery(id+"F2.wireOp",EDGE,"E9.0");var subQ2=makeQuery(id+"F2.imprint","INTERSECT",VERTEX,{"derivedFrom":[subQ1,subQ0]});Q2=makeQuery(id+"F2.imprint","IMPRINT",FACE,{"disambiguationData":[TD([[makeQuery(id+"F2.imprint","IMPRINT",EDGE,{"disambiguationData":[TD([[subQ2,-1.0]])],"derivedFrom":subQ1}),-1.0]])]});}
            var Q3;
            {var subQ0=sQuery(id+"F2.wireOp",EDGE,"E11");var subQ1=sQuery(id+"F2.wireOp",EDGE,"E9.0");var subQ2=makeQuery(id+"F2.imprint","INTERSECT",VERTEX,{"disambiguationData":[OD(0.0)],"derivedFrom":[subQ1,subQ0]});Q3=makeQuery(id+"F2.imprint","IMPRINT",FACE,{"disambiguationData":[TD([[makeQuery(id+"F2.imprint","IMPRINT",EDGE,{"disambiguationData":[TD([[subQ2,-1.0]])],"derivedFrom":subQ1}),-1.0]])]});}
            var Q4;
            {var subQ0=sQuery(id+"F2.wireOp",EDGE,"E12.3.0.0");var subQ1=sQuery(id+"F2.wireOp",EDGE,"E9.0");var subQ2=makeQuery(id+"F2.imprint","INTERSECT",VERTEX,{"disambiguationData":[OD(0.0)],"derivedFrom":[subQ1,subQ0]});Q4=makeQuery(id+"F2.imprint","IMPRINT",FACE,{"disambiguationData":[TD([[makeQuery(id+"F2.imprint","IMPRINT",EDGE,{"disambiguationData":[TD([[subQ2,-1.0]])],"derivedFrom":subQ1}),-1.0]])]});}
            var Q5;
            {var subQ0=sQuery(id+"F2.wireOp",EDGE,"E12.2.0.0");var subQ1=sQuery(id+"F2.wireOp",EDGE,"E9.0");var subQ2=makeQuery(id+"F2.imprint","INTERSECT",VERTEX,{"disambiguationData":[OD(0.0)],"derivedFrom":[subQ1,subQ0]});Q5=makeQuery(id+"F2.imprint","IMPRINT",FACE,{"disambiguationData":[TD([[makeQuery(id+"F2.imprint","IMPRINT",EDGE,{"disambiguationData":[TD([[subQ2,-1.0]])],"derivedFrom":subQ1}),-1.0]])]});}
            var Q6;
            {var subQ0=sQuery(id+"F2.wireOp",EDGE,"E12.3.0.0");var subQ1=sQuery(id+"F2.wireOp",EDGE,"E9.0");var subQ2=makeQuery(id+"F2.imprint","INTERSECT",VERTEX,{"disambiguationData":[OD(0.0)],"derivedFrom":[subQ1,subQ0]});Q6=makeQuery(id+"F2.imprint","IMPRINT",FACE,{"disambiguationData":[TD([[makeQuery(id+"F2.imprint","IMPRINT",EDGE,{"disambiguationData":[TD([[subQ2,-1.0]])],"derivedFrom":subQ1}),1.0]])]});}
            var Q7;
            {var subQ0=sQuery(id+"F2.wireOp",EDGE,"E12.2.0.0");var subQ1=sQuery(id+"F2.wireOp",EDGE,"E9.0");var subQ2=makeQuery(id+"F2.imprint","INTERSECT",VERTEX,{"disambiguationData":[OD(0.0)],"derivedFrom":[subQ1,subQ0]});Q7=makeQuery(id+"F2.imprint","IMPRINT",FACE,{"disambiguationData":[TD([[makeQuery(id+"F2.imprint","IMPRINT",EDGE,{"disambiguationData":[TD([[subQ2,-1.0]])],"derivedFrom":subQ1}),1.0]])]});}
            var Q8;
            {var subQ0=sQuery(id+"F2.wireOp",EDGE,"E12.1.0.0");var subQ1=sQuery(id+"F2.wireOp",EDGE,"E9.0");var subQ2=makeQuery(id+"F2.imprint","INTERSECT",VERTEX,{"disambiguationData":[OD(0.0)],"derivedFrom":[subQ1,subQ0]});Q8=makeQuery(id+"F2.imprint","IMPRINT",FACE,{"disambiguationData":[TD([[makeQuery(id+"F2.imprint","IMPRINT",EDGE,{"disambiguationData":[TD([[subQ2,-1.0]])],"derivedFrom":subQ1}),1.0]])]});}
            var Q9;
            {var subQ0=sQuery(id+"F2.wireOp",EDGE,"E12.1.0.0");var subQ1=sQuery(id+"F2.wireOp",EDGE,"E9.0");var subQ2=makeQuery(id+"F2.imprint","INTERSECT",VERTEX,{"disambiguationData":[OD(0.0)],"derivedFrom":[subQ1,subQ0]});Q9=makeQuery(id+"F2.imprint","IMPRINT",FACE,{"disambiguationData":[TD([[makeQuery(id+"F2.imprint","IMPRINT",EDGE,{"disambiguationData":[TD([[subQ2,-1.0]])],"derivedFrom":subQ1}),-1.0]])]});}
            var Q10;
            {var subQ0=sQuery(id+"F2.wireOp",EDGE,"E12.6.0.0");var subQ1=sQuery(id+"F2.wireOp",EDGE,"E9.0");var subQ2=makeQuery(id+"F2.imprint","INTERSECT",VERTEX,{"disambiguationData":[OD(0.0)],"derivedFrom":[subQ1,subQ0]});Q10=makeQuery(id+"F2.imprint","IMPRINT",FACE,{"disambiguationData":[TD([[makeQuery(id+"F2.imprint","IMPRINT",EDGE,{"disambiguationData":[TD([[subQ2,-1.0]])],"derivedFrom":subQ1}),1.0]])]});}
            var Q11;
            {var subQ0=sQuery(id+"F2.wireOp",EDGE,"E12.4.0.0");var subQ1=sQuery(id+"F2.wireOp",EDGE,"E9.0");var subQ2=makeQuery(id+"F2.imprint","INTERSECT",VERTEX,{"disambiguationData":[OD(0.0)],"derivedFrom":[subQ1,subQ0]});Q11=makeQuery(id+"F2.imprint","IMPRINT",FACE,{"disambiguationData":[TD([[makeQuery(id+"F2.imprint","IMPRINT",EDGE,{"disambiguationData":[TD([[subQ2,-1.0]])],"derivedFrom":subQ1}),1.0]])]});}
            var Q12;
            {var subQ0=sQuery(id+"F2.wireOp",EDGE,"E12.5.0.0");var subQ1=sQuery(id+"F2.wireOp",EDGE,"E9.0");var subQ2=makeQuery(id+"F2.imprint","INTERSECT",VERTEX,{"disambiguationData":[OD(0.0)],"derivedFrom":[subQ1,subQ0]});Q12=makeQuery(id+"F2.imprint","IMPRINT",FACE,{"disambiguationData":[TD([[makeQuery(id+"F2.imprint","IMPRINT",EDGE,{"disambiguationData":[TD([[subQ2,-1.0]])],"derivedFrom":subQ1}),1.0]])]});}
            var Q13;
            {var subQ0=sQuery(id+"F2.wireOp",EDGE,"E12.9.0.0");var subQ1=sQuery(id+"F2.wireOp",EDGE,"E9.0");var subQ2=makeQuery(id+"F2.imprint","INTERSECT",VERTEX,{"disambiguationData":[OD(0.0)],"derivedFrom":[subQ1,subQ0]});Q13=makeQuery(id+"F2.imprint","IMPRINT",FACE,{"disambiguationData":[TD([[makeQuery(id+"F2.imprint","IMPRINT",EDGE,{"disambiguationData":[TD([[subQ2,-1.0]])],"derivedFrom":subQ1}),1.0]])]});}
            var Q14;
            {var subQ0=sQuery(id+"F2.wireOp",EDGE,"E12.8.0.0");var subQ1=sQuery(id+"F2.wireOp",EDGE,"E9.0");var subQ2=makeQuery(id+"F2.imprint","INTERSECT",VERTEX,{"disambiguationData":[OD(0.0)],"derivedFrom":[subQ1,subQ0]});Q14=makeQuery(id+"F2.imprint","IMPRINT",FACE,{"disambiguationData":[TD([[makeQuery(id+"F2.imprint","IMPRINT",EDGE,{"disambiguationData":[TD([[subQ2,-1.0]])],"derivedFrom":subQ1}),-1.0]])]});}
            var Q15;
            {var subQ0=sQuery(id+"F2.wireOp",EDGE,"E12.12.0.0");var subQ1=sQuery(id+"F2.wireOp",EDGE,"E9.0");var subQ2=makeQuery(id+"F2.imprint","INTERSECT",VERTEX,{"disambiguationData":[OD(0.0)],"derivedFrom":[subQ1,subQ0]});Q15=makeQuery(id+"F2.imprint","IMPRINT",FACE,{"disambiguationData":[TD([[makeQuery(id+"F2.imprint","IMPRINT",EDGE,{"disambiguationData":[TD([[subQ2,-1.0]])],"derivedFrom":subQ1}),1.0]])]});}
            var Q16;
            {var subQ0=sQuery(id+"F2.wireOp",EDGE,"E12.4.0.0");var subQ1=sQuery(id+"F2.wireOp",EDGE,"E9.0");var subQ2=makeQuery(id+"F2.imprint","INTERSECT",VERTEX,{"disambiguationData":[OD(0.0)],"derivedFrom":[subQ1,subQ0]});Q16=makeQuery(id+"F2.imprint","IMPRINT",FACE,{"disambiguationData":[TD([[makeQuery(id+"F2.imprint","IMPRINT",EDGE,{"disambiguationData":[TD([[subQ2,-1.0]])],"derivedFrom":subQ1}),-1.0]])]});}
            var Q17;
            {var subQ0=sQuery(id+"F2.wireOp",EDGE,"E12.9.0.0");var subQ1=sQuery(id+"F2.wireOp",EDGE,"E9.0");var subQ2=makeQuery(id+"F2.imprint","INTERSECT",VERTEX,{"disambiguationData":[OD(0.0)],"derivedFrom":[subQ1,subQ0]});Q17=makeQuery(id+"F2.imprint","IMPRINT",FACE,{"disambiguationData":[TD([[makeQuery(id+"F2.imprint","IMPRINT",EDGE,{"disambiguationData":[TD([[subQ2,-1.0]])],"derivedFrom":subQ1}),-1.0]])]});}
            var Q18;
            {var subQ0=sQuery(id+"F2.wireOp",EDGE,"E12.11.0.0");var subQ1=sQuery(id+"F2.wireOp",EDGE,"E9.0");var subQ2=makeQuery(id+"F2.imprint","INTERSECT",VERTEX,{"disambiguationData":[OD(0.0)],"derivedFrom":[subQ1,subQ0]});Q18=makeQuery(id+"F2.imprint","IMPRINT",FACE,{"disambiguationData":[TD([[makeQuery(id+"F2.imprint","IMPRINT",EDGE,{"disambiguationData":[TD([[subQ2,-1.0]])],"derivedFrom":subQ1}),1.0]])]});}
            var Q19;
            {var subQ0=sQuery(id+"F2.wireOp",EDGE,"E12.7.0.0");var subQ1=sQuery(id+"F2.wireOp",EDGE,"E9.0");var subQ2=makeQuery(id+"F2.imprint","INTERSECT",VERTEX,{"disambiguationData":[OD(0.0)],"derivedFrom":[subQ1,subQ0]});Q19=makeQuery(id+"F2.imprint","IMPRINT",FACE,{"disambiguationData":[TD([[makeQuery(id+"F2.imprint","IMPRINT",EDGE,{"disambiguationData":[TD([[subQ2,-1.0]])],"derivedFrom":subQ1}),1.0]])]});}
            var Q20;
            {var subQ0=sQuery(id+"F2.wireOp",EDGE,"E12.10.0.0");var subQ1=sQuery(id+"F2.wireOp",EDGE,"E9.0");var subQ2=makeQuery(id+"F2.imprint","INTERSECT",VERTEX,{"disambiguationData":[OD(0.0)],"derivedFrom":[subQ1,subQ0]});Q20=makeQuery(id+"F2.imprint","IMPRINT",FACE,{"disambiguationData":[TD([[makeQuery(id+"F2.imprint","IMPRINT",EDGE,{"disambiguationData":[TD([[subQ2,-1.0]])],"derivedFrom":subQ1}),-1.0]])]});}
            var Q21;
            {var subQ0=sQuery(id+"F2.wireOp",EDGE,"E12.12.0.0");var subQ1=sQuery(id+"F2.wireOp",EDGE,"E9.0");var subQ2=makeQuery(id+"F2.imprint","INTERSECT",VERTEX,{"disambiguationData":[OD(0.0)],"derivedFrom":[subQ1,subQ0]});Q21=makeQuery(id+"F2.imprint","IMPRINT",FACE,{"disambiguationData":[TD([[makeQuery(id+"F2.imprint","IMPRINT",EDGE,{"disambiguationData":[TD([[subQ2,-1.0]])],"derivedFrom":subQ1}),-1.0]])]});}
            var Q22;
            {var subQ0=sQuery(id+"F2.wireOp",EDGE,"E12.8.0.0");var subQ1=sQuery(id+"F2.wireOp",EDGE,"E9.0");var subQ2=makeQuery(id+"F2.imprint","INTERSECT",VERTEX,{"disambiguationData":[OD(0.0)],"derivedFrom":[subQ1,subQ0]});Q22=makeQuery(id+"F2.imprint","IMPRINT",FACE,{"disambiguationData":[TD([[makeQuery(id+"F2.imprint","IMPRINT",EDGE,{"disambiguationData":[TD([[subQ2,-1.0]])],"derivedFrom":subQ1}),1.0]])]});}
            var Q23;
            {var subQ0=sQuery(id+"F2.wireOp",EDGE,"E12.13.0.0");var subQ1=sQuery(id+"F2.wireOp",EDGE,"E9.0");var subQ2=makeQuery(id+"F2.imprint","INTERSECT",VERTEX,{"disambiguationData":[OD(0.0)],"derivedFrom":[subQ1,subQ0]});Q23=makeQuery(id+"F2.imprint","IMPRINT",FACE,{"disambiguationData":[TD([[makeQuery(id+"F2.imprint","IMPRINT",EDGE,{"disambiguationData":[TD([[subQ2,-1.0]])],"derivedFrom":subQ1}),1.0]])]});}
            var Q24;
            {var subQ0=sQuery(id+"F2.wireOp",EDGE,"E12.6.0.0");var subQ1=sQuery(id+"F2.wireOp",EDGE,"E9.0");var subQ2=makeQuery(id+"F2.imprint","INTERSECT",VERTEX,{"disambiguationData":[OD(0.0)],"derivedFrom":[subQ1,subQ0]});Q24=makeQuery(id+"F2.imprint","IMPRINT",FACE,{"disambiguationData":[TD([[makeQuery(id+"F2.imprint","IMPRINT",EDGE,{"disambiguationData":[TD([[subQ2,-1.0]])],"derivedFrom":subQ1}),-1.0]])]});}
            var Q25;
            {var subQ0=sQuery(id+"F2.wireOp",EDGE,"E12.13.0.0");var subQ1=sQuery(id+"F2.wireOp",EDGE,"E9.0");var subQ2=makeQuery(id+"F2.imprint","INTERSECT",VERTEX,{"disambiguationData":[OD(0.0)],"derivedFrom":[subQ1,subQ0]});Q25=makeQuery(id+"F2.imprint","IMPRINT",FACE,{"disambiguationData":[TD([[makeQuery(id+"F2.imprint","IMPRINT",EDGE,{"disambiguationData":[TD([[subQ2,-1.0]])],"derivedFrom":subQ1}),-1.0]])]});}
            var Q26;
            {var subQ0=sQuery(id+"F2.wireOp",EDGE,"E12.10.0.0");var subQ1=sQuery(id+"F2.wireOp",EDGE,"E9.0");var subQ2=makeQuery(id+"F2.imprint","INTERSECT",VERTEX,{"disambiguationData":[OD(0.0)],"derivedFrom":[subQ1,subQ0]});Q26=makeQuery(id+"F2.imprint","IMPRINT",FACE,{"disambiguationData":[TD([[makeQuery(id+"F2.imprint","IMPRINT",EDGE,{"disambiguationData":[TD([[subQ2,-1.0]])],"derivedFrom":subQ1}),1.0]])]});}
            var Q27;
            {var subQ0=sQuery(id+"F2.wireOp",EDGE,"E12.5.0.0");var subQ1=sQuery(id+"F2.wireOp",EDGE,"E9.0");var subQ2=makeQuery(id+"F2.imprint","INTERSECT",VERTEX,{"disambiguationData":[OD(0.0)],"derivedFrom":[subQ1,subQ0]});Q27=makeQuery(id+"F2.imprint","IMPRINT",FACE,{"disambiguationData":[TD([[makeQuery(id+"F2.imprint","IMPRINT",EDGE,{"disambiguationData":[TD([[subQ2,-1.0]])],"derivedFrom":subQ1}),-1.0]])]});}
            var Q28;
            {var subQ0=sQuery(id+"F2.wireOp",EDGE,"E12.7.0.0");var subQ1=sQuery(id+"F2.wireOp",EDGE,"E9.0");var subQ2=makeQuery(id+"F2.imprint","INTERSECT",VERTEX,{"disambiguationData":[OD(0.0)],"derivedFrom":[subQ1,subQ0]});Q28=makeQuery(id+"F2.imprint","IMPRINT",FACE,{"disambiguationData":[TD([[makeQuery(id+"F2.imprint","IMPRINT",EDGE,{"disambiguationData":[TD([[subQ2,-1.0]])],"derivedFrom":subQ1}),-1.0]])]});}
            var Q29;
            {var subQ0=sQuery(id+"F2.wireOp",EDGE,"E12.11.0.0");var subQ1=sQuery(id+"F2.wireOp",EDGE,"E9.0");var subQ2=makeQuery(id+"F2.imprint","INTERSECT",VERTEX,{"disambiguationData":[OD(0.0)],"derivedFrom":[subQ1,subQ0]});Q29=makeQuery(id+"F2.imprint","IMPRINT",FACE,{"disambiguationData":[TD([[makeQuery(id+"F2.imprint","IMPRINT",EDGE,{"disambiguationData":[TD([[subQ2,-1.0]])],"derivedFrom":subQ1}),-1.0]])]});}
            var Q30;
            {var subQ0=sQuery(id+"F2.wireOp",EDGE,"E12.16.0.0");var subQ1=sQuery(id+"F2.wireOp",EDGE,"E9.0");var subQ2=makeQuery(id+"F2.imprint","INTERSECT",VERTEX,{"disambiguationData":[OD(0.0)],"derivedFrom":[subQ1,subQ0]});Q30=makeQuery(id+"F2.imprint","IMPRINT",FACE,{"disambiguationData":[TD([[makeQuery(id+"F2.imprint","IMPRINT",EDGE,{"disambiguationData":[TD([[subQ2,-1.0]])],"derivedFrom":subQ1}),-1.0]])]});}
            var Q31;
            {var subQ0=sQuery(id+"F2.wireOp",EDGE,"E12.15.0.0");var subQ1=sQuery(id+"F2.wireOp",EDGE,"E9.0");var subQ2=makeQuery(id+"F2.imprint","INTERSECT",VERTEX,{"disambiguationData":[OD(0.0)],"derivedFrom":[subQ1,subQ0]});Q31=makeQuery(id+"F2.imprint","IMPRINT",FACE,{"disambiguationData":[TD([[makeQuery(id+"F2.imprint","IMPRINT",EDGE,{"disambiguationData":[TD([[subQ2,-1.0]])],"derivedFrom":subQ1}),1.0]])]});}
            var Q32;
            {var subQ0=sQuery(id+"F2.wireOp",EDGE,"E12.18.0.0");var subQ1=sQuery(id+"F2.wireOp",EDGE,"E9.0");var subQ2=makeQuery(id+"F2.imprint","INTERSECT",VERTEX,{"disambiguationData":[OD(0.0)],"derivedFrom":[subQ1,subQ0]});Q32=makeQuery(id+"F2.imprint","IMPRINT",FACE,{"disambiguationData":[TD([[makeQuery(id+"F2.imprint","IMPRINT",EDGE,{"disambiguationData":[TD([[subQ2,-1.0]])],"derivedFrom":subQ1}),-1.0]])]});}
            var Q33;
            {var subQ0=sQuery(id+"F2.wireOp",EDGE,"E12.17.0.0");var subQ1=sQuery(id+"F2.wireOp",EDGE,"E9.0");var subQ2=makeQuery(id+"F2.imprint","INTERSECT",VERTEX,{"disambiguationData":[OD(0.0)],"derivedFrom":[subQ1,subQ0]});Q33=makeQuery(id+"F2.imprint","IMPRINT",FACE,{"disambiguationData":[TD([[makeQuery(id+"F2.imprint","IMPRINT",EDGE,{"disambiguationData":[TD([[subQ2,-1.0]])],"derivedFrom":subQ1}),-1.0]])]});}
            var Q34;
            {var subQ0=sQuery(id+"F2.wireOp",EDGE,"E12.15.0.0");var subQ1=sQuery(id+"F2.wireOp",EDGE,"E9.0");var subQ2=makeQuery(id+"F2.imprint","INTERSECT",VERTEX,{"disambiguationData":[OD(0.0)],"derivedFrom":[subQ1,subQ0]});Q34=makeQuery(id+"F2.imprint","IMPRINT",FACE,{"disambiguationData":[TD([[makeQuery(id+"F2.imprint","IMPRINT",EDGE,{"disambiguationData":[TD([[subQ2,-1.0]])],"derivedFrom":subQ1}),-1.0]])]});}
            var Q35;
            {var subQ0=sQuery(id+"F2.wireOp",EDGE,"E12.18.0.0");var subQ1=sQuery(id+"F2.wireOp",EDGE,"E9.0");var subQ2=makeQuery(id+"F2.imprint","INTERSECT",VERTEX,{"disambiguationData":[OD(0.0)],"derivedFrom":[subQ1,subQ0]});Q35=makeQuery(id+"F2.imprint","IMPRINT",FACE,{"disambiguationData":[TD([[makeQuery(id+"F2.imprint","IMPRINT",EDGE,{"disambiguationData":[TD([[subQ2,-1.0]])],"derivedFrom":subQ1}),1.0]])]});}
            var Q36;
            {var subQ0=sQuery(id+"F2.wireOp",EDGE,"E12.16.0.0");var subQ1=sQuery(id+"F2.wireOp",EDGE,"E9.0");var subQ2=makeQuery(id+"F2.imprint","INTERSECT",VERTEX,{"disambiguationData":[OD(0.0)],"derivedFrom":[subQ1,subQ0]});Q36=makeQuery(id+"F2.imprint","IMPRINT",FACE,{"disambiguationData":[TD([[makeQuery(id+"F2.imprint","IMPRINT",EDGE,{"disambiguationData":[TD([[subQ2,-1.0]])],"derivedFrom":subQ1}),1.0]])]});}
            var Q37;
            {var subQ0=sQuery(id+"F2.wireOp",EDGE,"E12.14.0.0");var subQ1=sQuery(id+"F2.wireOp",EDGE,"E9.0");var subQ2=makeQuery(id+"F2.imprint","INTERSECT",VERTEX,{"disambiguationData":[OD(0.0)],"derivedFrom":[subQ1,subQ0]});Q37=makeQuery(id+"F2.imprint","IMPRINT",FACE,{"disambiguationData":[TD([[makeQuery(id+"F2.imprint","IMPRINT",EDGE,{"disambiguationData":[TD([[subQ2,-1.0]])],"derivedFrom":subQ1}),1.0]])]});}
            var Q38;
            {var subQ0=sQuery(id+"F2.wireOp",EDGE,"E12.14.0.0");var subQ1=sQuery(id+"F2.wireOp",EDGE,"E9.0");var subQ2=makeQuery(id+"F2.imprint","INTERSECT",VERTEX,{"disambiguationData":[OD(0.0)],"derivedFrom":[subQ1,subQ0]});Q38=makeQuery(id+"F2.imprint","IMPRINT",FACE,{"disambiguationData":[TD([[makeQuery(id+"F2.imprint","IMPRINT",EDGE,{"disambiguationData":[TD([[subQ2,-1.0]])],"derivedFrom":subQ1}),-1.0]])]});}
            var Q39;
            {var subQ0=sQuery(id+"F2.wireOp",EDGE,"E12.17.0.0");var subQ1=sQuery(id+"F2.wireOp",EDGE,"E9.0");var subQ2=makeQuery(id+"F2.imprint","INTERSECT",VERTEX,{"disambiguationData":[OD(0.0)],"derivedFrom":[subQ1,subQ0]});Q39=makeQuery(id+"F2.imprint","IMPRINT",FACE,{"disambiguationData":[TD([[makeQuery(id+"F2.imprint","IMPRINT",EDGE,{"disambiguationData":[TD([[subQ2,-1.0]])],"derivedFrom":subQ1}),1.0]])]});}
            extrude(context, id + "F4", {"entities" : qUnion([Q0, Q1, Q2, Q3, Q4, Q5, Q6, Q7, Q8, Q9, Q10, Q11, Q12, Q13, Q14, Q15, Q16, Q17, Q18, Q19, Q20, Q21, Q22, Q23, Q24, Q25, Q26, Q27, Q28, Q29, Q30, Q31, Q32, Q33, Q34, Q35, Q36, Q37, Q38, Q39]), "operationType" : NewBodyOperationType.ADD, "oppositeDirection" : true, "depth" : 997.6 * mm});
        }
    });
